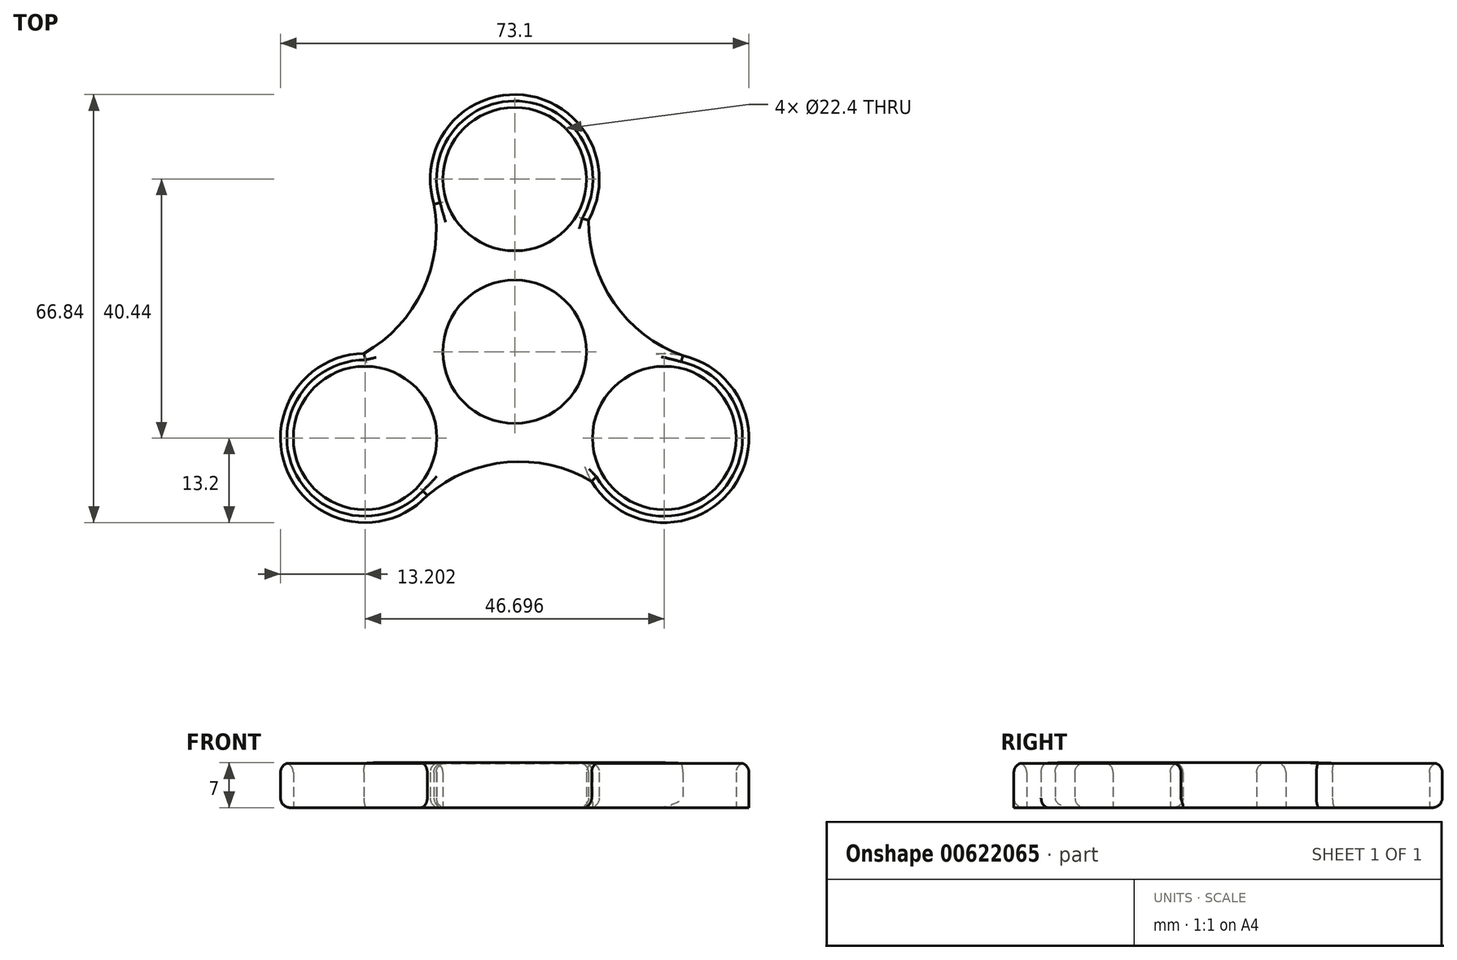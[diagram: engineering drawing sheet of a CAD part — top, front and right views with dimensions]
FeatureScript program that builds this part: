
annotation { "Feature Type Name" : "Feature", "Feature Type Description" : "" }
export const myFeature = defineFeature(function(context is Context, id is Id, definition is map)
    precondition{}
    {
        {
            var Q0;
            Q0=qCreatedBy(makeId("Top.planeOp"),FACE);
            var sketch = newSketch(context, id + "F0", { "sketchPlane" : qUnion([Q0])});
            skCircle(sketch, "E0", {"center": v(0, 0) * mm, "radius": 11.2 * mm});
            skCircle(sketch, "E1", {"center": v(0, 26.96) * mm, "radius": 11.2 * mm});
            skArc(sketch, "E2", {"start": v(11.53, 20.53) * mm, "mid": v(1.36, 40.09) * mm, "end": v(-12.6, 23.03) * mm});
            skCircle(sketch, "E3.1.0", {"center": v(-23.35, -13.48) * mm, "radius": 11.2 * mm});
            skArc(sketch, "E3.1.1", {"start": v(-23.54, -0.28) * mm, "mid": v(-35.4, -18.86) * mm, "end": v(-13.65, -22.43) * mm});
            skCircle(sketch, "E3.2.0", {"center": v(23.35, -13.48) * mm, "radius": 11.2 * mm});
            skArc(sketch, "E3.2.1", {"start": v(12.01, -20.25) * mm, "mid": v(34.04, -21.23) * mm, "end": v(26.25, -0.6) * mm});
            skArc(sketch, "E4", {"start": v(-23.54, -0.28) * mm, "mid": v(-14.34, 9.63) * mm, "end": v(-12.6, 23.03) * mm});
            skArc(sketch, "E5.1.0", {"start": v(12.01, -20.25) * mm, "mid": v(-1.17, -17.24) * mm, "end": v(-13.65, -22.43) * mm});
            skArc(sketch, "E5.2.0", {"start": v(11.53, 20.53) * mm, "mid": v(15.5, 7.6) * mm, "end": v(26.25, -0.6) * mm});
            skSolve(sketch);
        }
        {
            var Q0;
            Q0=makeQuery(id+"F0.imprint","IMPRINT",FACE,{"disambiguationData":[TD([[makeQuery(id+"F0.imprint","IMPRINT",EDGE,{"derivedFrom":sQuery(id+"F0.wireOp",EDGE,"E0")}),-1.0]])]});
            extrude(context, id + "F1", {"entities" : qUnion([Q0]), "depth" : 7 * mm, "offsetDistance" : 25 * mm});
        }
        {
            var Q0;
            Q0=makeQuery(id+"F1.opExtrude","CAP_FACE",FACE,{"disambiguationData":[OSD([sQuery(id+"F0.wireOp",EDGE,"E0"),sQuery(id+"F0.wireOp",EDGE,"E1"),sQuery(id+"F0.wireOp",EDGE,"E2"),sQuery(id+"F0.wireOp",EDGE,"E3.1.0"),sQuery(id+"F0.wireOp",EDGE,"E3.1.1"),sQuery(id+"F0.wireOp",EDGE,"E3.2.0"),sQuery(id+"F0.wireOp",EDGE,"E3.2.1"),sQuery(id+"F0.wireOp",EDGE,"E4"),sQuery(id+"F0.wireOp",EDGE,"E5.1.0"),sQuery(id+"F0.wireOp",EDGE,"E5.2.0")])],"isStart":false});
            var Q1;
            Q1=makeQuery(id+"F1.opExtrude","CAP_EDGE",EDGE,{"disambiguationData":[OSD([sQuery(id+"F0.wireOp",EDGE,"E5.1.0")])],"isStart":true});
            var Q2;
            Q2=makeQuery(id+"F1.opExtrude","CAP_EDGE",EDGE,{"disambiguationData":[OSD([sQuery(id+"F0.wireOp",EDGE,"E3.2.1")])],"isStart":false});
            var Q3;
            Q3=makeQuery(id+"F1.opExtrude","CAP_EDGE",EDGE,{"disambiguationData":[OSD([sQuery(id+"F0.wireOp",EDGE,"E5.2.0")])],"isStart":true});
            var Q4;
            Q4=makeQuery(id+"F1.opExtrude","CAP_EDGE",EDGE,{"disambiguationData":[OSD([sQuery(id+"F0.wireOp",EDGE,"E2")])],"isStart":true});
            var Q5;
            Q5=makeQuery(id+"F1.opExtrude","CAP_EDGE",EDGE,{"disambiguationData":[OSD([sQuery(id+"F0.wireOp",EDGE,"E3.1.1")])],"isStart":true});
            var Q6;
            Q6=makeQuery(id+"F1.opExtrude","CAP_EDGE",EDGE,{"disambiguationData":[OSD([sQuery(id+"F0.wireOp",EDGE,"E4")])],"isStart":true});
            fillet(context, id + "F2", {"entities" : qUnion([Q0, Q1, Q2, Q3, Q4, Q5, Q6]), "radius" : 1.5 * mm, "tangentPropagation" : true, "allowEdgeOverflow" : false});
        }
    });
